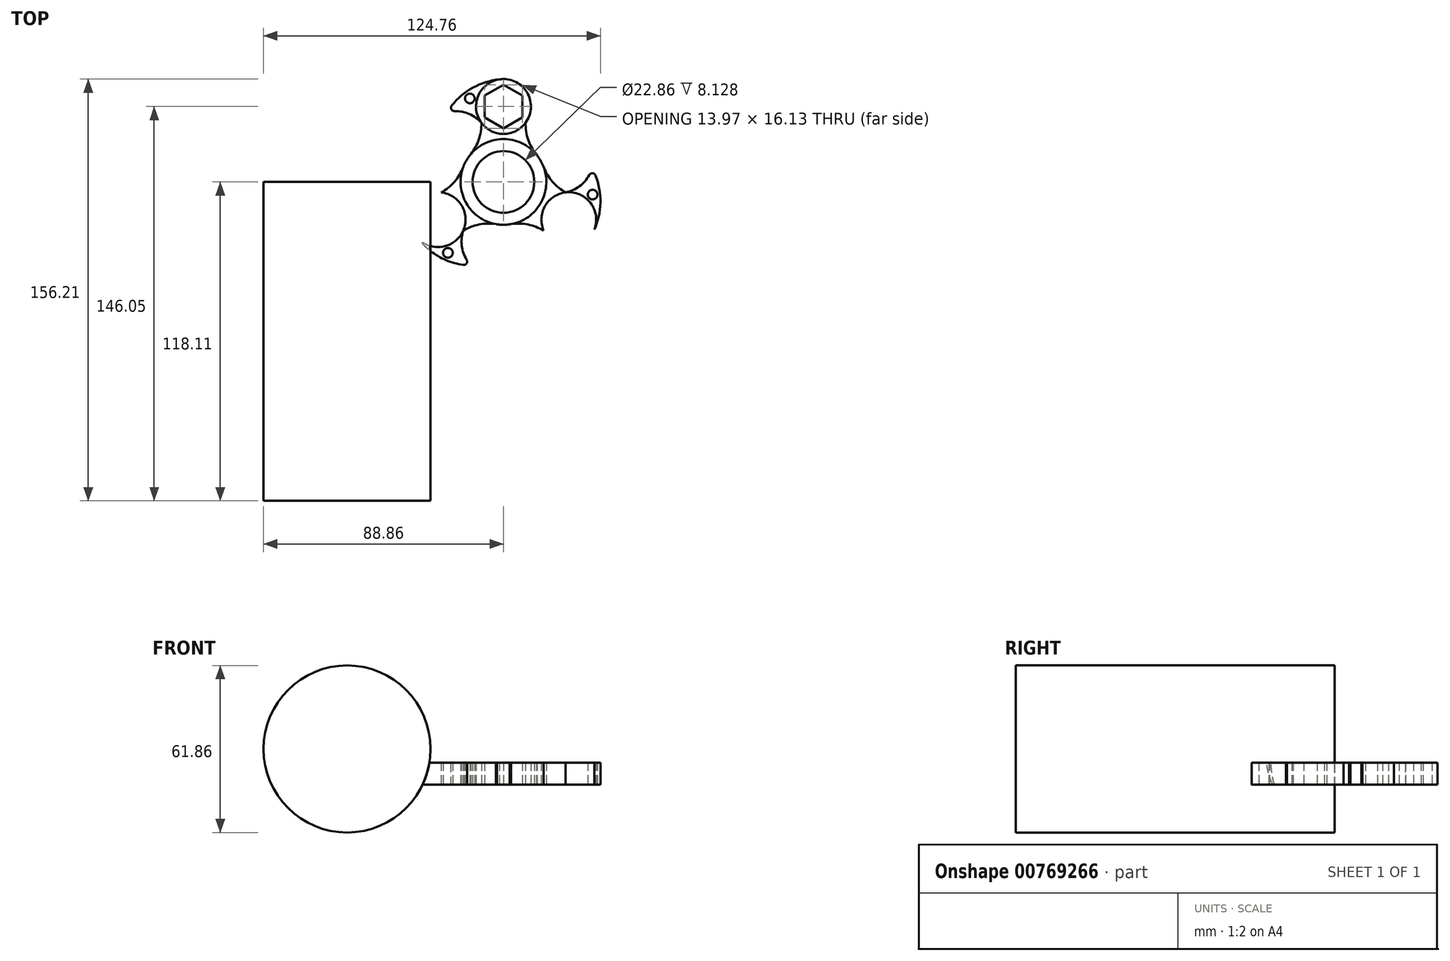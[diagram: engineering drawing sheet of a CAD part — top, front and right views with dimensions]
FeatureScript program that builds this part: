
annotation { "Feature Type Name" : "Feature", "Feature Type Description" : "" }
export const myFeature = defineFeature(function(context is Context, id is Id, definition is map)
    precondition{}
    {
        {
            var Q0;
            Q0=qCreatedBy(makeId("Top.planeOp"),FACE);
            var sketch = newSketch(context, id + "F0", { "sketchPlane" : qUnion([Q0])});
            skCircle(sketch, "E0", {"center": v(0, 0) * mm, "radius": 38.1 * mm});
            skCircle(sketch, "E1", {"center": v(0, 0) * mm, "radius": 11.43 * mm});
            skCircle(sketch, "E2.cCircle", {"center": v(0, 27.94) * mm, "radius": 8.07 * mm, "construction": true});
            skLineSegment(sketch, "E2.0", {"start": v(0, 36) * mm, "end": v(6.99, 31.97) * mm});
            skLineSegment(sketch, "E2.1", {"start": v(6.99, 31.97) * mm, "end": v(6.99, 23.9) * mm});
            skLineSegment(sketch, "E2.2", {"start": v(6.99, 23.9) * mm, "end": v(0, 19.87) * mm});
            skLineSegment(sketch, "E2.3", {"start": v(0, 19.87) * mm, "end": v(-6.99, 23.9) * mm});
            skLineSegment(sketch, "E2.4", {"start": v(-6.99, 23.9) * mm, "end": v(-6.98, 31.97) * mm});
            skLineSegment(sketch, "E2.5", {"start": v(-6.99, 31.97) * mm, "end": v(0, 36) * mm});
            skCircle(sketch, "E3", {"center": v(0, 27.94) * mm, "radius": 10.16 * mm});
            skCircle(sketch, "E4", {"center": v(0, 0) * mm, "radius": 15.88 * mm});
            skArc(sketch, "E5", {"start": v(8.16, 21.9) * mm, "mid": v(9.21, 15.5) * mm, "end": v(12.42, 9.88) * mm});
            skPoint(sketch, "E5.startSnap0", {"position": v(-3.5, 21.9) * mm});
            skArc(sketch, "E6", {"start": v(-12.42, 9.88) * mm, "mid": v(-9.2, 15.5) * mm, "end": v(-8.16, 21.9) * mm});
            skArc(sketch, "E7", {"start": v(0, 38.1) * mm, "mid": v(-11.95, 34.56) * mm, "end": v(-20.88, 25.87) * mm});
            skArc(sketch, "E8", {"start": v(-8.16, 21.9) * mm, "mid": v(-13.97, 25.66) * mm, "end": v(-20.88, 25.87) * mm});
            skCircle(sketch, "E9", {"center": v(-12.45, 30.94) * mm, "radius": 1.79 * mm});
            skArc(sketch, "E10.1.0", {"start": v(-14.88, -18.01) * mm, "mid": v(-15.24, -24.93) * mm, "end": v(-11.96, -31.02) * mm});
            skArc(sketch, "E10.1.1", {"start": v(-2.35, -15.7) * mm, "mid": v(-8.82, -15.72) * mm, "end": v(-14.88, -18.01) * mm});
            skArc(sketch, "E10.1.2", {"start": v(-33, -19.05) * mm, "mid": v(-23.95, -27.63) * mm, "end": v(-11.96, -31.02) * mm});
            skCircle(sketch, "E10.1.3", {"center": v(-24.2, -13.97) * mm, "radius": 10.16 * mm});
            skArc(sketch, "E10.1.4", {"start": v(-23.04, -3.88) * mm, "mid": v(-18.03, 0.23) * mm, "end": v(-14.77, 5.82) * mm});
            skCircle(sketch, "E10.1.5", {"center": v(-20.57, -26.26) * mm, "radius": 1.79 * mm});
            skLineSegment(sketch, "E10.1.6", {"start": v(-17.21, -18) * mm, "end": v(-24.2, -22.04) * mm});
            skLineSegment(sketch, "E10.1.7", {"start": v(-24.2, -22.04) * mm, "end": v(-31.18, -18) * mm});
            skLineSegment(sketch, "E10.1.8", {"start": v(-31.18, -18) * mm, "end": v(-31.18, -9.94) * mm});
            skLineSegment(sketch, "E10.1.9", {"start": v(-31.18, -9.94) * mm, "end": v(-24.2, -5.9) * mm});
            skLineSegment(sketch, "E10.1.10", {"start": v(-24.2, -5.9) * mm, "end": v(-17.21, -9.94) * mm});
            skLineSegment(sketch, "E10.1.11", {"start": v(-17.21, -9.94) * mm, "end": v(-17.21, -18) * mm});
            skArc(sketch, "E10.2.0", {"start": v(23.04, -3.88) * mm, "mid": v(29.2, -0.73) * mm, "end": v(32.84, 5.15) * mm});
            skArc(sketch, "E10.2.1", {"start": v(14.77, 5.82) * mm, "mid": v(18.02, 0.22) * mm, "end": v(23.04, -3.88) * mm});
            skArc(sketch, "E10.2.2", {"start": v(33, -19.05) * mm, "mid": v(35.9, -6.93) * mm, "end": v(32.84, 5.15) * mm});
            skCircle(sketch, "E10.2.3", {"center": v(24.2, -13.97) * mm, "radius": 10.16 * mm});
            skArc(sketch, "E10.2.4", {"start": v(14.88, -18.01) * mm, "mid": v(8.82, -15.73) * mm, "end": v(2.35, -15.7) * mm});
            skCircle(sketch, "E10.2.5", {"center": v(33.03, -4.69) * mm, "radius": 1.79 * mm});
            skLineSegment(sketch, "E10.2.6", {"start": v(24.2, -5.9) * mm, "end": v(31.18, -9.94) * mm});
            skLineSegment(sketch, "E10.2.7", {"start": v(31.18, -9.94) * mm, "end": v(31.18, -18) * mm});
            skLineSegment(sketch, "E10.2.8", {"start": v(31.18, -18) * mm, "end": v(24.2, -22.04) * mm});
            skLineSegment(sketch, "E10.2.9", {"start": v(24.2, -22.04) * mm, "end": v(17.21, -18) * mm});
            skLineSegment(sketch, "E10.2.10", {"start": v(17.21, -18) * mm, "end": v(17.21, -9.94) * mm});
            skLineSegment(sketch, "E10.2.11", {"start": v(17.21, -9.94) * mm, "end": v(24.2, -5.9) * mm});
            skSolve(sketch);
        }
        {
            var Q0;
            {var subQ0=sQuery(id+"F0.wireOp",EDGE,"E5");Q0=makeQuery(id+"F0.imprint","IMPRINT",FACE,{"disambiguationData":[TD([[makeQuery(id+"F0.imprint","IMPRINT",EDGE,{"derivedFrom":subQ0}),-1.0]])]});}
            var Q1;
            Q1=makeQuery(id+"F0.imprint","IMPRINT",FACE,{"disambiguationData":[TD([[makeQuery(id+"F0.imprint","IMPRINT",EDGE,{"derivedFrom":sQuery(id+"F0.wireOp",EDGE,"E2.0")}),1.0]])]});
            var Q2;
            {var subQ0=sQuery(id+"F0.wireOp",EDGE,"E8");Q2=makeQuery(id+"F0.imprint","IMPRINT",FACE,{"disambiguationData":[TD([[makeQuery(id+"F0.imprint","IMPRINT",EDGE,{"derivedFrom":subQ0}),-1.0]])]});}
            var Q3;
            Q3=makeQuery(id+"F0.imprint","IMPRINT",FACE,{"disambiguationData":[TD([[makeQuery(id+"F0.imprint","IMPRINT",EDGE,{"derivedFrom":sQuery(id+"F0.wireOp",EDGE,"E1")}),-1.0]])]});
            var Q4;
            Q4=makeQuery(id+"F0.imprint","IMPRINT",FACE,{"disambiguationData":[TD([[makeQuery(id+"F0.imprint","IMPRINT",EDGE,{"derivedFrom":sQuery(id+"F0.wireOp",EDGE,"E10.1.6")}),1.0]])]});
            var Q5;
            {var subQ0=sQuery(id+"F0.wireOp",EDGE,"E10.1.1");Q5=makeQuery(id+"F0.imprint","IMPRINT",FACE,{"disambiguationData":[TD([[makeQuery(id+"F0.imprint","IMPRINT",EDGE,{"derivedFrom":subQ0}),-1.0]])]});}
            var Q6;
            {var subQ1=sQuery(id+"F0.wireOp",EDGE,"E10.1.0");Q6=makeQuery(id+"F0.imprint","IMPRINT",FACE,{"disambiguationData":[TD([[makeQuery(id+"F0.imprint","IMPRINT",EDGE,{"derivedFrom":subQ1}),-1.0]])]});}
            var Q7;
            {var subQ0=sQuery(id+"F0.wireOp",EDGE,"E10.2.1");Q7=makeQuery(id+"F0.imprint","IMPRINT",FACE,{"disambiguationData":[TD([[makeQuery(id+"F0.imprint","IMPRINT",EDGE,{"derivedFrom":subQ0}),-1.0]])]});}
            var Q8;
            Q8=makeQuery(id+"F0.imprint","IMPRINT",FACE,{"disambiguationData":[TD([[makeQuery(id+"F0.imprint","IMPRINT",EDGE,{"derivedFrom":sQuery(id+"F0.wireOp",EDGE,"E10.2.6")}),1.0]])]});
            var Q9;
            {var subQ1=sQuery(id+"F0.wireOp",EDGE,"E10.2.0");Q9=makeQuery(id+"F0.imprint","IMPRINT",FACE,{"disambiguationData":[TD([[makeQuery(id+"F0.imprint","IMPRINT",EDGE,{"derivedFrom":subQ1}),-1.0]])]});}
            extrude(context, id + "F1", {"entities" : qUnion([Q0, Q1, Q2, Q3, Q4, Q5, Q6, Q7, Q8, Q9]), "depth" : 8.13 * mm, "offsetDistance" : 25.4 * mm});
        }
        {
            var Q0;
            Q0=makeQuery(id+"F1.opExtrude","SWEPT_EDGE",EDGE,{"disambiguationData":[OSD([sQuery(id+"F0.wireOp",EDGE,"E7"),sQuery(id+"F0.wireOp",EDGE,"E8")])]});
            var Q1;
            Q1=makeQuery(id+"F1.opExtrude","SWEPT_EDGE",EDGE,{"disambiguationData":[OSD([sQuery(id+"F0.wireOp",EDGE,"E10.1.0"),sQuery(id+"F0.wireOp",EDGE,"E10.1.2")])]});
            var Q2;
            Q2=makeQuery(id+"F1.opExtrude","SWEPT_EDGE",EDGE,{"disambiguationData":[OSD([sQuery(id+"F0.wireOp",EDGE,"E10.2.0"),sQuery(id+"F0.wireOp",EDGE,"E10.2.2")])]});
            fillet(context, id + "F2", {"entities" : qUnion([Q0, Q1, Q2]), "radius" : 1.27 * mm, "tangentPropagation" : true, "allowEdgeOverflow" : false});
        }
        {
            var Q0;
            Q0=qCreatedBy(makeId("Front.planeOp"),FACE);
            var sketch = newSketch(context, id + "F3", { "sketchPlane" : qUnion([Q0])});
            skCircle(sketch, "E11", {"center": v(-57.93, 13.22) * mm, "radius": 30.93 * mm});
            skSolve(sketch);
        }
        {
            var Q0;
            Q0 = qSketchRegion(id + "F3", true);
            extrude(context, id + "F4", {"entities" : qUnion([Q0]), "operationType" : NewBodyOperationType.ADD, "depth" : 118.1 * mm, "offsetDistance" : 25.4 * mm});
        }
    });
